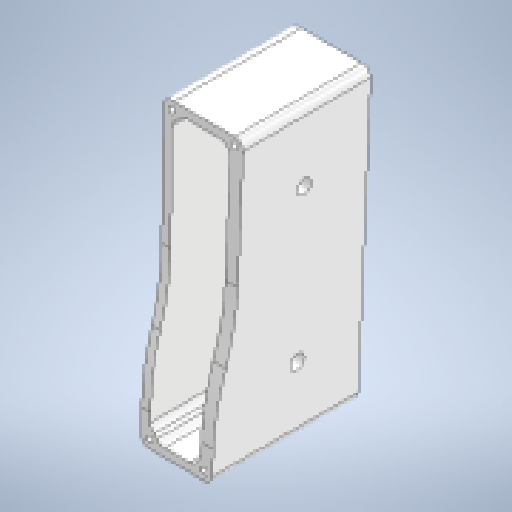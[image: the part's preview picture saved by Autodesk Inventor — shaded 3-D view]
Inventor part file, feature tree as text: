
AUTODESK INVENTOR PART (.ipt)
format: ipt  version: 2025.1 (Build 291241000, 241)  size: 233,984 bytes
history: native  units: mm
features: other x7, reference x4, sketch x3, extrude x3, fillet x2, projected_geometry x2
ambient origin geometry x8: Origin, YZ Plane, XZ Plane, XY Plane, X Axis, Y Axis, Z Axis, Center Point
bodies: Body1 (feature_tree)
feature tree (21):
  other  "ソリッド1"
  sketch  "スケッチ1"
  other  "作業平面1"
  extrude  "押し出し1"  Depth=1.6mm
  sketch  "スケッチ2"
  other  "作業平面2"
  extrude  "押し出し2"  Depth=1.6mm
  fillet  "フィレット1"  Radius=1.6mm
  extrude  "押し出し3"  Depth=1.6mm
  fillet  "フィレット2"  Radius=4.0mm
  reference  "参照1"
  reference  "参照2"
  reference  "参照3"
  reference  "参照4"
  projected_geometry  "投影ループ1"
  sketch  "スケッチ3"
  projected_geometry  "投影ループ2"
  other  "<userpath>\Documents\Inventor\Vixen\doutai.iam"
  other  "doutai.iam"
  other  "newnewude:3"
  other  "newnewude_2:3"
